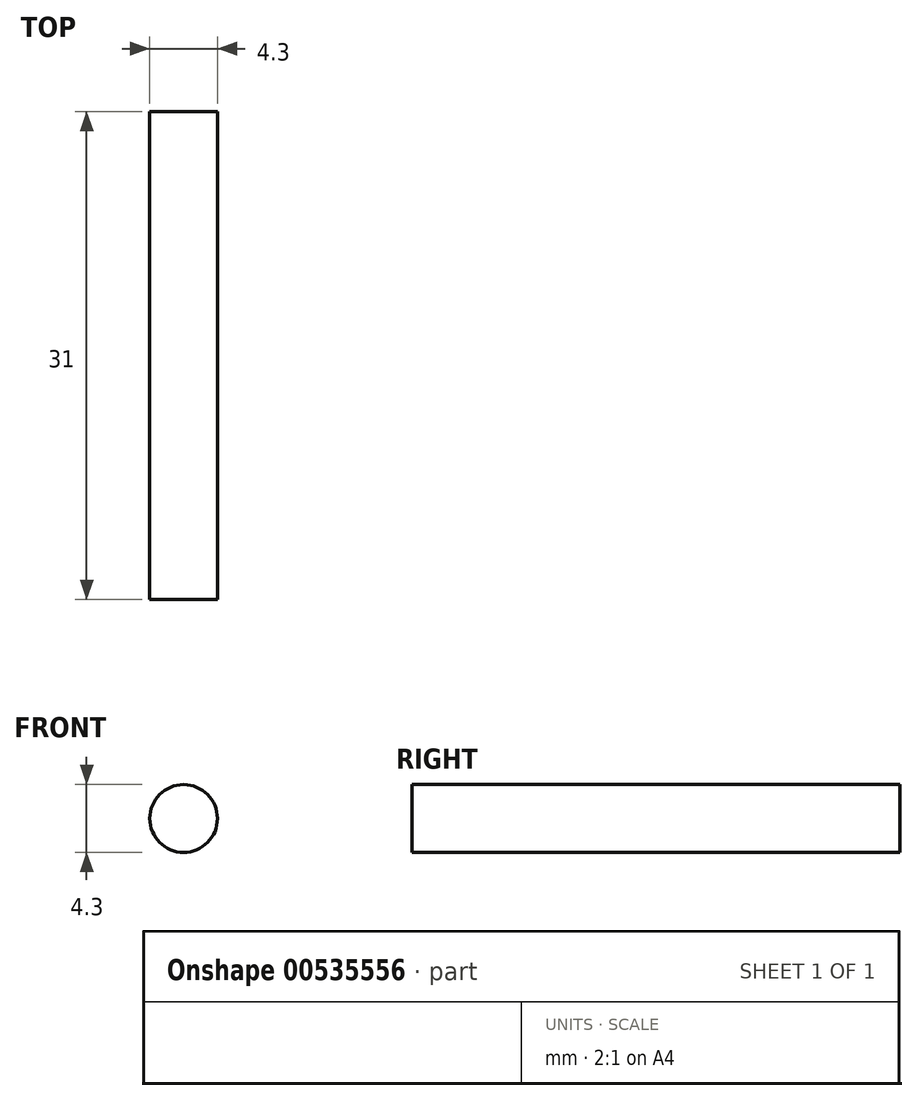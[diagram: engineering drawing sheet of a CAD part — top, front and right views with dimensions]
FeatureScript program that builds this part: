
annotation { "Feature Type Name" : "Feature", "Feature Type Description" : "" }
export const myFeature = defineFeature(function(context is Context, id is Id, definition is map)
    precondition{}
    {
        {
            var Q0;
            Q0=qCreatedBy(makeId("Front.planeOp"),FACE);
            var sketch = newSketch(context, id + "F0", { "sketchPlane" : qUnion([Q0])});
            skCircle(sketch, "E0", {"center": v(0, 0) * mm, "radius": 2.15 * mm});
            skSolve(sketch);
        }
        {
            var Q0;
            Q0 = qSketchRegion(id + "F0", true);
            extrude(context, id + "F1", {"entities" : qUnion([Q0]), "depth" : 31 * mm, "offsetDistance" : 25 * mm});
        }
    });
